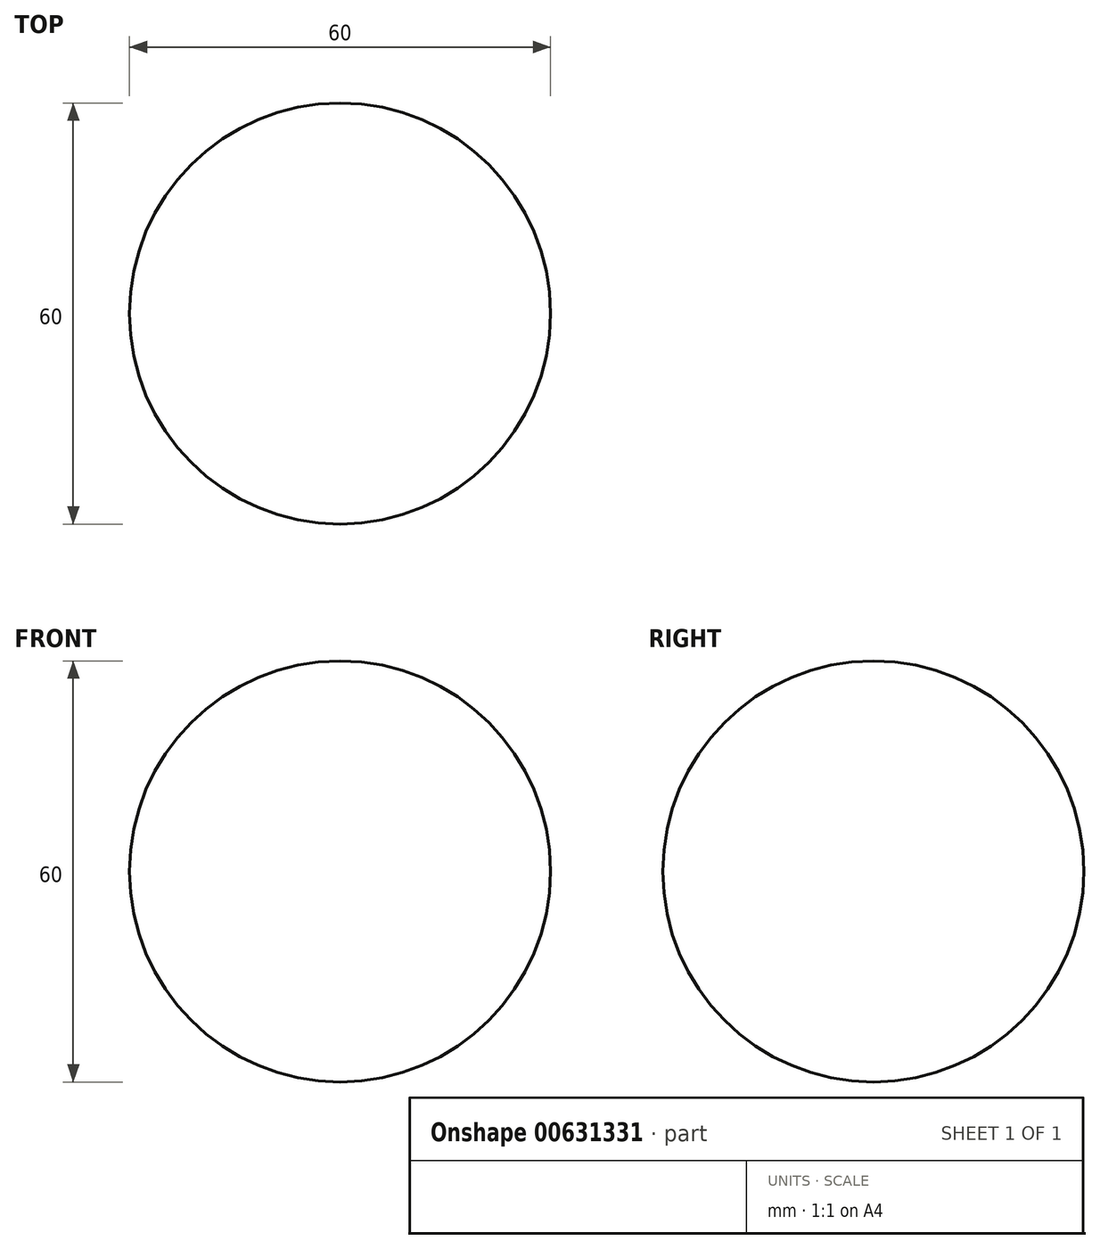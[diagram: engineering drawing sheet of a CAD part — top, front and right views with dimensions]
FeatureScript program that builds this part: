
annotation { "Feature Type Name" : "Feature", "Feature Type Description" : "" }
export const myFeature = defineFeature(function(context is Context, id is Id, definition is map)
    precondition{}
    {
        {
            var Q0;
            Q0=qCreatedBy(makeId("Front.planeOp"),FACE);
            var sketch = newSketch(context, id + "F0", { "sketchPlane" : qUnion([Q0])});
            skArc(sketch, "E0", {"start": v(0, -30) * mm, "mid": v(30, 0) * mm, "end": v(0, 30) * mm});
            skLineSegment(sketch, "E1", {"start": v(0, 30) * mm, "end": v(0, -30) * mm});
            skSolve(sketch);
        }
        {
            var Q0;
            Q0=makeQuery(id+"F0.imprint","IMPRINT",FACE,{"disambiguationData":[TD([[makeQuery(id+"F0.imprint","IMPRINT",EDGE,{"derivedFrom":sQuery(id+"F0.wireOp",EDGE,"E0")}),1.0]])]});
            var Q1;
            Q1=sQuery(id+"F0.wireOp",EDGE,"E1");
            revolve(context, id + "F1", {"entities" : qUnion([Q0]), "axis" : qUnion([Q1]), "revolveType" : RevolveType.FULL});
        }
    });
